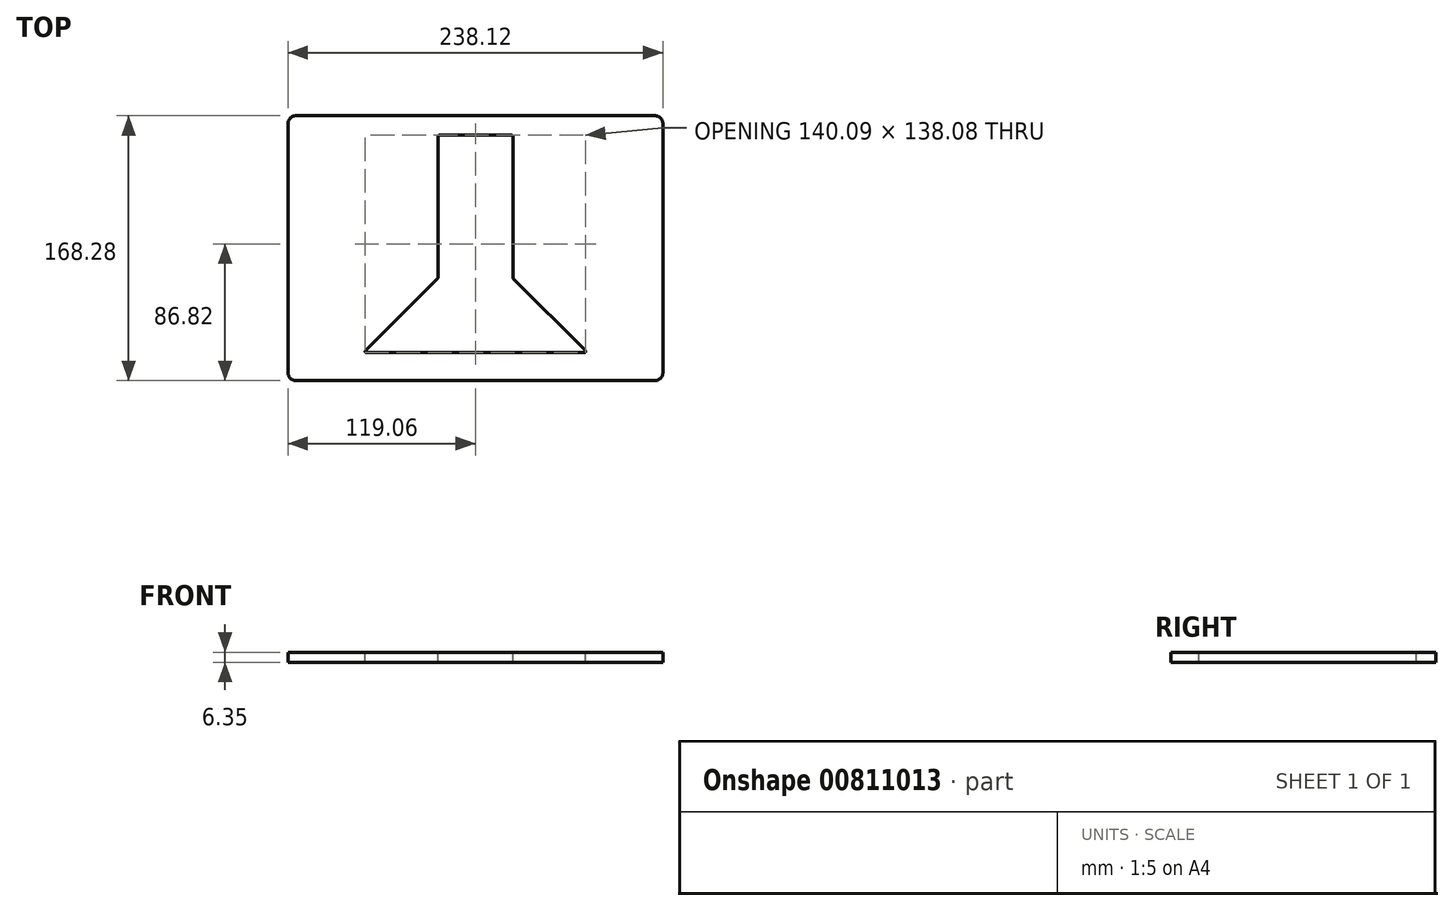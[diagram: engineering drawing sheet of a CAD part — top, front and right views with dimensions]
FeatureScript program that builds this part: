
annotation { "Feature Type Name" : "Feature", "Feature Type Description" : "" }
export const myFeature = defineFeature(function(context is Context, id is Id, definition is map)
    precondition{}
    {
        {
            var Q0;
            Q0=qCreatedBy(makeId("Top.planeOp"),FACE);
            var sketch = newSketch(context, id + "F0", { "sketchPlane" : qUnion([Q0])});
            skLineSegment(sketch, "E0.bottom", {"start": v(-113.98, 84.14) * mm, "end": v(113.98, 84.14) * mm});
            skLineSegment(sketch, "E0.top", {"start": v(-113.98, -84.14) * mm, "end": v(113.98, -84.14) * mm});
            skLineSegment(sketch, "E0.left", {"start": v(-119.06, 79.06) * mm, "end": v(-119.06, -79.06) * mm});
            skLineSegment(sketch, "E0.right", {"start": v(119.06, 79.06) * mm, "end": v(119.06, -79.06) * mm});
            skPoint(sketch, "E0.middle", {"position": v(0, 0) * mm});
            skPoint(sketch, "E1.visualSharp", {"position": v(-119.06, 84.14) * mm});
            skArc(sketch, "E1.filletArc", {"start": v(-113.98, 84.14) * mm, "mid": v(-117.57, 82.65) * mm, "end": v(-119.06, 79.06) * mm});
            skPoint(sketch, "E2.visualSharp", {"position": v(-119.06, -84.14) * mm});
            skArc(sketch, "E2.filletArc", {"start": v(-119.06, -79.06) * mm, "mid": v(-117.57, -82.65) * mm, "end": v(-113.98, -84.14) * mm});
            skPoint(sketch, "E3.visualSharp", {"position": v(119.06, -84.14) * mm});
            skArc(sketch, "E3.filletArc", {"start": v(113.98, -84.14) * mm, "mid": v(117.57, -82.65) * mm, "end": v(119.06, -79.06) * mm});
            skPoint(sketch, "E4.visualSharp", {"position": v(119.06, 84.14) * mm});
            skArc(sketch, "E4.filletArc", {"start": v(119.06, 79.06) * mm, "mid": v(117.57, 82.65) * mm, "end": v(113.98, 84.14) * mm});
            skSolve(sketch);
        }
        {
            var Q0;
            Q0 = qSketchRegion(id + "F0", true);
            extrude(context, id + "F1", {"entities" : qUnion([Q0]), "depth" : 6.35 * mm, "offsetDistance" : 25.4 * mm});
        }
        {
            var Q0;
            Q0=makeQuery(id+"F1.opExtrude","CAP_FACE",FACE,{"disambiguationData":[OSD([sQuery(id+"F0.wireOp",EDGE,"E0.bottom"),sQuery(id+"F0.wireOp",EDGE,"E0.top"),sQuery(id+"F0.wireOp",EDGE,"E0.left"),sQuery(id+"F0.wireOp",EDGE,"E0.right"),sQuery(id+"F0.wireOp",EDGE,"E1.filletArc"),sQuery(id+"F0.wireOp",EDGE,"E2.filletArc"),sQuery(id+"F0.wireOp",EDGE,"E3.filletArc"),sQuery(id+"F0.wireOp",EDGE,"E4.filletArc")])],"isStart":false});
            var sketch = newSketch(context, id + "F2", { "sketchPlane" : qUnion([Q0])});
            skLineSegment(sketch, "E5", {"start": v(0, 70.45) * mm, "end": v(-22.48, 70.45) * mm});
            skLineSegment(sketch, "E6", {"start": v(-22.48, 70.45) * mm, "end": v(-22.48, -19.47) * mm});
            skLineSegment(sketch, "E7", {"start": v(-22.48, -19.47) * mm, "end": v(-68.1, -65.09) * mm});
            skLineSegment(sketch, "E8", {"start": v(-68.1, -65.09) * mm, "end": v(0, -65.09) * mm});
            skLineSegment(sketch, "E9.MirrorCS", {"start": v(0, 70.45) * mm, "end": v(22.48, 70.45) * mm});
            skLineSegment(sketch, "E10.MirrorCS", {"start": v(22.48, 70.45) * mm, "end": v(22.48, -19.47) * mm});
            skLineSegment(sketch, "E11.MirrorCS", {"start": v(22.48, -19.47) * mm, "end": v(68.1, -65.09) * mm});
            skLineSegment(sketch, "E12.MirrorCS", {"start": v(68.1, -65.09) * mm, "end": v(0, -65.09) * mm});
            skSolve(sketch);
        }
        {
            var Q0;
            Q0 = qSketchRegion(id + "F2", true);
            extrude(context, id + "F3", {"entities" : qUnion([Q0]), "operationType" : NewBodyOperationType.REMOVE, "oppositeDirection" : true, "depth" : 25.4 * mm, "offsetDistance" : 25.4 * mm});
        }
        {
            var Q0;
            Q0=makeQuery(id+"F1.opExtrude","CAP_FACE",FACE,{"disambiguationData":[OSD([sQuery(id+"F0.wireOp",EDGE,"E0.bottom"),sQuery(id+"F0.wireOp",EDGE,"E0.top"),sQuery(id+"F0.wireOp",EDGE,"E0.left"),sQuery(id+"F0.wireOp",EDGE,"E0.right"),sQuery(id+"F0.wireOp",EDGE,"E1.filletArc"),sQuery(id+"F0.wireOp",EDGE,"E2.filletArc"),sQuery(id+"F0.wireOp",EDGE,"E3.filletArc"),sQuery(id+"F0.wireOp",EDGE,"E4.filletArc")])],"isStart":false});
            var sketch = newSketch(context, id + "F4", { "sketchPlane" : qUnion([Q0])});
            skLineSegment(sketch, "E13.0", {"start": v(-23.75, 70.93) * mm, "end": v(-23.75, -18.62) * mm});
            skLineSegment(sketch, "E13.1", {"start": v(23.75, 70.93) * mm, "end": v(23.75, -18.62) * mm});
            skLineSegment(sketch, "E13.2", {"start": v(23.98, -19.17) * mm, "end": v(69.82, -65.01) * mm});
            skLineSegment(sketch, "E13.3", {"start": v(-22.96, 71.72) * mm, "end": v(22.96, 71.72) * mm});
            skLineSegment(sketch, "E13.4", {"start": v(69.26, -66.36) * mm, "end": v(-69.26, -66.36) * mm});
            skLineSegment(sketch, "E13.5", {"start": v(-23.98, -19.17) * mm, "end": v(-69.82, -65.01) * mm});
            skPoint(sketch, "E14.visualSharp", {"position": v(-23.75, 71.72) * mm});
            skArc(sketch, "E14.filletArc", {"start": v(-22.96, 71.72) * mm, "mid": v(-23.52, 71.49) * mm, "end": v(-23.75, 70.93) * mm});
            skPoint(sketch, "E15.visualSharp", {"position": v(23.75, 71.72) * mm});
            skArc(sketch, "E15.filletArc", {"start": v(23.75, 70.93) * mm, "mid": v(23.52, 71.49) * mm, "end": v(22.96, 71.72) * mm});
            skPoint(sketch, "E16.visualSharp", {"position": v(23.75, -18.94) * mm});
            skArc(sketch, "E16.filletArc", {"start": v(23.75, -18.62) * mm, "mid": v(23.8, -18.92) * mm, "end": v(23.98, -19.17) * mm});
            skPoint(sketch, "E17.visualSharp", {"position": v(71.16, -66.36) * mm});
            skArc(sketch, "E17.filletArc", {"start": v(69.26, -66.36) * mm, "mid": v(70, -65.87) * mm, "end": v(69.82, -65.01) * mm});
            skPoint(sketch, "E18.visualSharp", {"position": v(-71.16, -66.36) * mm});
            skArc(sketch, "E18.filletArc", {"start": v(-69.82, -65.01) * mm, "mid": v(-70, -65.87) * mm, "end": v(-69.26, -66.36) * mm});
            skPoint(sketch, "E19.visualSharp", {"position": v(-23.75, -18.94) * mm});
            skArc(sketch, "E19.filletArc", {"start": v(-23.98, -19.17) * mm, "mid": v(-23.8, -18.92) * mm, "end": v(-23.75, -18.62) * mm});
            skSolve(sketch);
        }
        {
            var Q0;
            Q0 = qSketchRegion(id + "F4", true);
            extrude(context, id + "F5", {"entities" : qUnion([Q0]), "operationType" : NewBodyOperationType.REMOVE, "oppositeDirection" : true, "depth" : 25.4 * mm, "offsetDistance" : 25.4 * mm});
        }
    });
